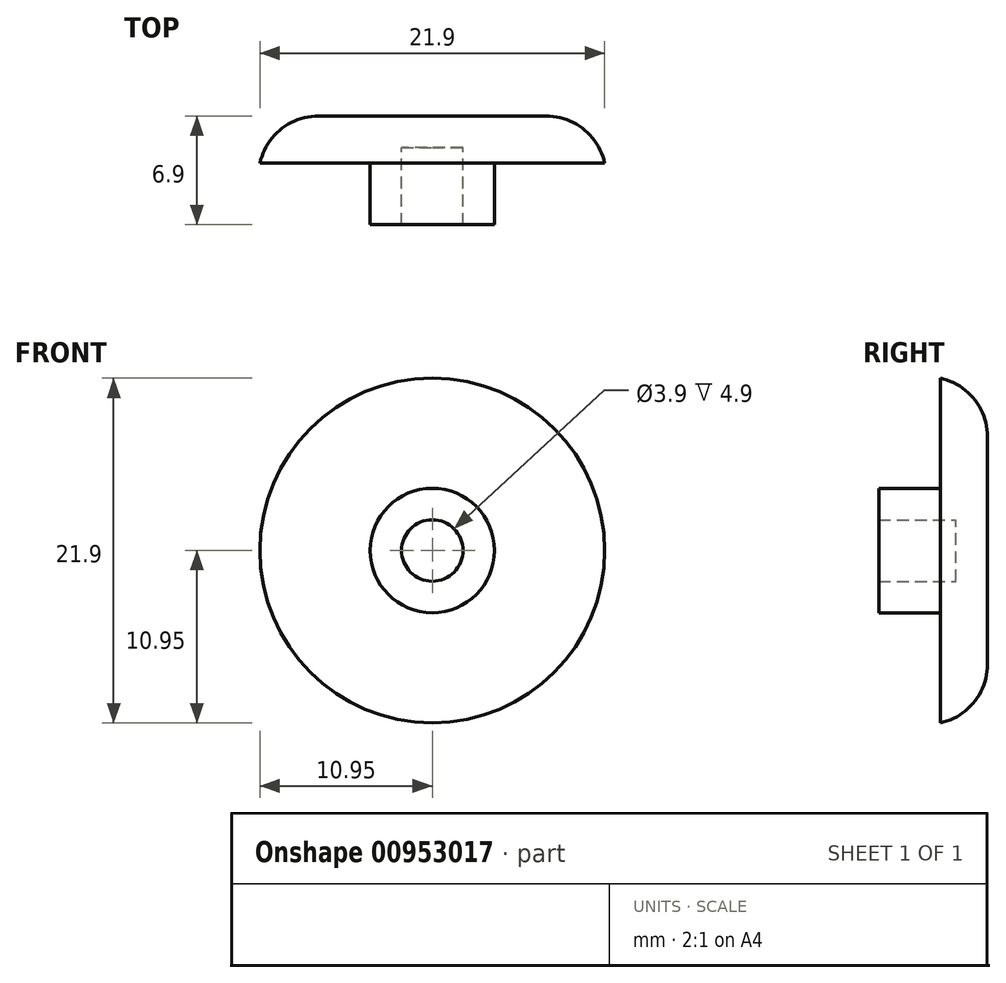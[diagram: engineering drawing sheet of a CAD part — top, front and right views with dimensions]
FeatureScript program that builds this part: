
annotation { "Feature Type Name" : "Feature", "Feature Type Description" : "" }
export const myFeature = defineFeature(function(context is Context, id is Id, definition is map)
    precondition{}
    {
        {
            var Q0;
            Q0=qCreatedBy(makeId("Front.planeOp"),FACE);
            var sketch = newSketch(context, id + "F0", { "sketchPlane" : qUnion([Q0])});
            skCircle(sketch, "E0", {"center": v(0, 0) * mm, "radius": 10.95 * mm});
            skSolve(sketch);
        }
        {
            var Q0;
            Q0=makeQuery(id+"F0.imprint","IMPRINT",FACE,{"disambiguationData":[TD([[makeQuery(id+"F0.imprint","IMPRINT",EDGE,{"derivedFrom":sQuery(id+"F0.wireOp",EDGE,"E0")}),1.0]])]});
            extrude(context, id + "F1", {"entities" : qUnion([Q0]), "depth" : 3 * mm, "offsetDistance" : 25.4 * mm});
        }
        {
            var Q0;
            Q0=qCreatedBy(makeId("Front.planeOp"),FACE);
            var sketch = newSketch(context, id + "F2", { "sketchPlane" : qUnion([Q0])});
            skCircle(sketch, "E1", {"center": v(0, 0) * mm, "radius": 3.95 * mm});
            skSolve(sketch);
        }
        {
            var Q0;
            Q0=makeQuery(id+"F2.imprint","IMPRINT",FACE,{"disambiguationData":[TD([[makeQuery(id+"F2.imprint","IMPRINT",EDGE,{"derivedFrom":sQuery(id+"F2.wireOp",EDGE,"E1")}),1.0]])]});
            extrude(context, id + "F3", {"entities" : qUnion([Q0]), "operationType" : NewBodyOperationType.ADD, "depth" : 6.9 * mm, "offsetDistance" : 25.4 * mm});
        }
        {
            var Q0;
            Q0=makeQuery(id+"F3.opExtrude","CAP_FACE",FACE,{"disambiguationData":[OSD([sQuery(id+"F2.wireOp",EDGE,"E1")])],"isStart":false});
            shell(context, id + "F4", {"entities" : qUnion([Q0]), "thickness" : 2 * mm});
        }
        {
            var Q0;
            Q0=makeQuery(id+"F1.opExtrude","CAP_FACE",FACE,{"disambiguationData":[OSD([sQuery(id+"F0.wireOp",EDGE,"E0")])],"isStart":true});
            fillet(context, id + "F5", {"entities" : qUnion([Q0]), "radius" : 3.8 * mm, "tangentPropagation" : true, "allowEdgeOverflow" : false});
        }
    });
